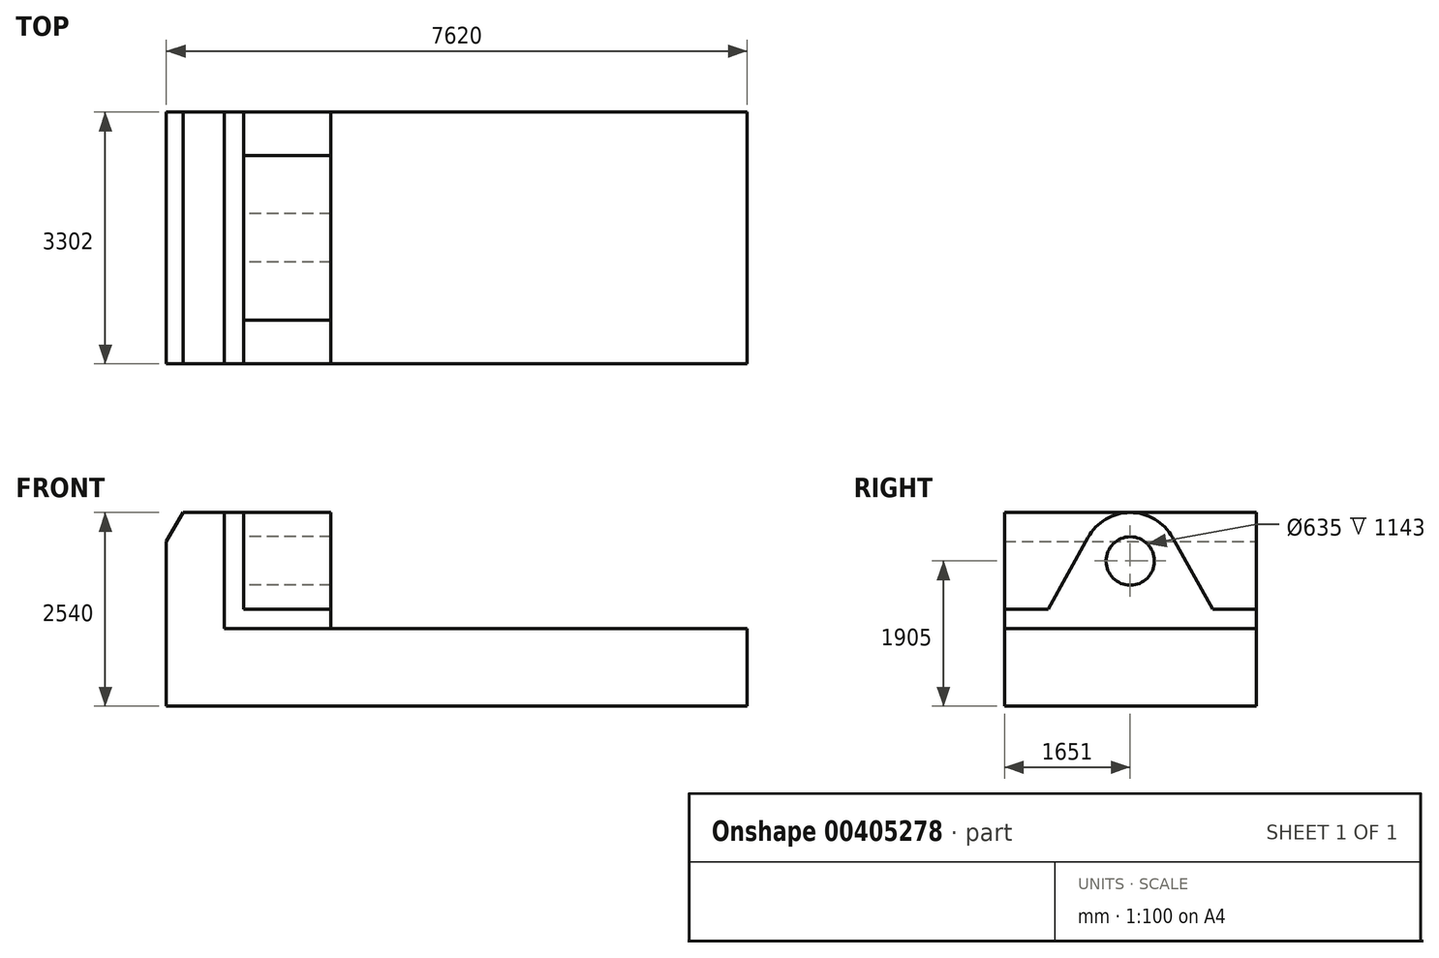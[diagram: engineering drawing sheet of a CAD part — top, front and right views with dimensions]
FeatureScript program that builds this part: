
annotation { "Feature Type Name" : "Feature", "Feature Type Description" : "" }
export const myFeature = defineFeature(function(context is Context, id is Id, definition is map)
    precondition{}
    {
        {
            var Q0;
            Q0=qCreatedBy(makeId("Front.planeOp"),FACE);
            var sketch = newSketch(context, id + "F0", { "sketchPlane" : qUnion([Q0])});
            skLineSegment(sketch, "E0.bottom", {"start": v(0, 0) * mm, "end": v(-7620, 0) * mm});
            skLineSegment(sketch, "E0.top", {"start": v(0, 1016) * mm, "end": v(-7620, 1016) * mm});
            skLineSegment(sketch, "E0.left", {"start": v(0, 0) * mm, "end": v(0, 1016) * mm});
            skLineSegment(sketch, "E0.right", {"start": v(-7620, 0) * mm, "end": v(-7620, 1016) * mm});
            skLineSegment(sketch, "E1.bottom", {"start": v(-7620, 1016) * mm, "end": v(-6858, 1016) * mm});
            skLineSegment(sketch, "E1.top", {"start": v(-7620, 2540) * mm, "end": v(-6858, 2540) * mm});
            skLineSegment(sketch, "E1.left", {"start": v(-7620, 1016) * mm, "end": v(-7620, 2540) * mm});
            skLineSegment(sketch, "E1.right", {"start": v(-6858, 1016) * mm, "end": v(-6858, 2540) * mm});
            skSolve(sketch);
        }
        {
            var Q0;
            Q0 = qSketchRegion(id + "F0", true);
            extrude(context, id + "F1", {"entities" : qUnion([Q0]), "depth" : 3302 * mm});
        }
        {
            var Q0;
            Q0=makeQuery(id+"F1.opExtrude","SWEPT_EDGE",EDGE,{"disambiguationData":[OSD([sQuery(id+"F0.wireOp",EDGE,"E1.top"),sQuery(id+"F0.wireOp",EDGE,"E1.left")])]});
            chamfer(context, id + "F2", {"entities" : qUnion([Q0]), "chamferType" : ChamferType.OFFSET_ANGLE, "width" : 381 * mm, "oppositeDirection" : false, "angle" : 30 * degree, "tangentPropagation" : true});
        }
        {
            var Q0;
            Q0=makeQuery(id+"F1.opExtrude","CAP_FACE",FACE,{"disambiguationData":[OSD([sQuery(id+"F0.wireOp",EDGE,"E0.bottom"),sQuery(id+"F0.wireOp",EDGE,"E0.top"),sQuery(id+"F0.wireOp",EDGE,"E0.left"),sQuery(id+"F0.wireOp",EDGE,"E0.right"),sQuery(id+"F0.wireOp",EDGE,"E1.top"),sQuery(id+"F0.wireOp",EDGE,"E1.left"),sQuery(id+"F0.wireOp",EDGE,"E1.right")])],"isStart":false});
            var sketch = newSketch(context, id + "F3", { "sketchPlane" : qUnion([Q0])});
            skLineSegment(sketch, "E2.bottom", {"start": v(-6858, 2540) * mm, "end": v(-6604, 2540) * mm});
            skLineSegment(sketch, "E2.top", {"start": v(-6858, 1016) * mm, "end": v(-6604, 1016) * mm});
            skLineSegment(sketch, "E2.left", {"start": v(-6858, 2540) * mm, "end": v(-6858, 1016) * mm});
            skLineSegment(sketch, "E2.right", {"start": v(-6604, 2540) * mm, "end": v(-6604, 1016) * mm});
            skLineSegment(sketch, "E3.bottom", {"start": v(-6604, 1016) * mm, "end": v(-5461, 1016) * mm});
            skLineSegment(sketch, "E3.top", {"start": v(-6604, 1270) * mm, "end": v(-5461, 1270) * mm});
            skLineSegment(sketch, "E3.left", {"start": v(-6604, 1016) * mm, "end": v(-6604, 1270) * mm});
            skLineSegment(sketch, "E3.right", {"start": v(-5461, 1016) * mm, "end": v(-5461, 1270) * mm});
            skSolve(sketch);
        }
        {
            var Q0;
            Q0=makeQuery(id+"F3.imprint","IMPRINT",FACE,{"disambiguationData":[TD([[makeQuery(id+"F3.imprint","IMPRINT",EDGE,{"derivedFrom":sQuery(id+"F3.wireOp",EDGE,"E2.bottom")}),-1.0]])]});
            var Q1;
            Q1=makeQuery(id+"F3.imprint","IMPRINT",FACE,{"disambiguationData":[TD([[makeQuery(id+"F3.imprint","IMPRINT",EDGE,{"derivedFrom":sQuery(id+"F3.wireOp",EDGE,"E3.bottom")}),-1.0]])]});
            extrude(context, id + "F4", {"entities" : qUnion([Q0, Q1]), "oppositeDirection" : true, "depth" : 3302 * mm});
        }
        {
            var Q0;
            Q0=makeQuery(id+"F4.opExtrude","SWEPT_FACE",FACE,{"disambiguationData":[OSD([sQuery(id+"F3.wireOp",EDGE,"E2.right")])]});
            var sketch = newSketch(context, id + "F5", { "sketchPlane" : qUnion([Q0])});
            skCircle(sketch, "E4", {"center": v(-1651, 1905) * mm, "radius": 635 * mm});
            skLineSegment(sketch, "E5", {"start": v(-2730.5, 1270) * mm, "end": v(-2206.01, 2213.52) * mm});
            skLineSegment(sketch, "E6.MirrorCS", {"start": v(-571.5, 1270) * mm, "end": v(-1095.99, 2213.52) * mm});
            skCircle(sketch, "E7", {"center": v(-1651, 1905) * mm, "radius": 317.5 * mm});
            skSolve(sketch);
        }
        {
            var Q0;
            {var subQ0=sQuery(id+"F5.wireOp",EDGE,"E6.MirrorCS");Q0=makeQuery(id+"F5.imprint","IMPRINT",FACE,{"disambiguationData":[TD([[makeQuery(id+"F5.imprint","IMPRINT",EDGE,{"derivedFrom":subQ0}),1.0]])]});}
            var Q1;
            {var subQ0=sQuery(id+"F5.wireOp",EDGE,"E5");Q1=makeQuery(id+"F5.imprint","IMPRINT",FACE,{"disambiguationData":[TD([[makeQuery(id+"F5.imprint","IMPRINT",EDGE,{"derivedFrom":subQ0}),-1.0]])]});}
            var Q2;
            Q2=makeQuery(id+"F5.imprint","IMPRINT",FACE,{"disambiguationData":[TD([[makeQuery(id+"F5.imprint","IMPRINT",EDGE,{"derivedFrom":sQuery(id+"F5.wireOp",EDGE,"E7")}),-1.0]])]});
            extrude(context, id + "F6", {"entities" : qUnion([Q0, Q1, Q2]), "operationType" : NewBodyOperationType.ADD, "depth" : 1143 * mm});
        }
    });
